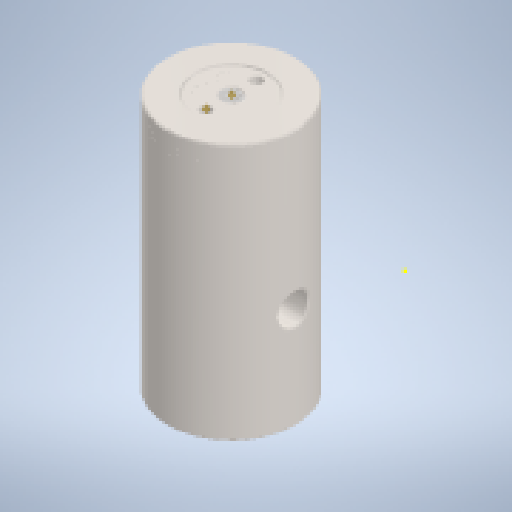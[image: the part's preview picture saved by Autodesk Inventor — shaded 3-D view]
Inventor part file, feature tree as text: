
AUTODESK INVENTOR PART (.ipt)
format: ipt  version: 2023 (Build 270158000, 158)  size: 1,771,008 bytes
history: native  units: mm
features: other x6, sketch x1, thread x1
ambient origin geometry x8: Origin, YZ Plane, XZ Plane, XY Plane, X Axis, Y Axis, Z Axis, Center Point
bodies: Solid1 (feature_tree)
feature tree (8):
  sketch  "Sketch1"
  other  "Work Point1"
  other  "Work Point2"
  other  "Work Point3"
  other  "Work Point4"
  other  "Work Point5"
  other  "Work Axis1"
  thread  "Thread2"  [1 undecoded]
note: 1 required parameter value undecoded (feature->parameter linkage not recoverable at this tier; creation-order binding heuristic only, values carry confidence <= 0.55)
